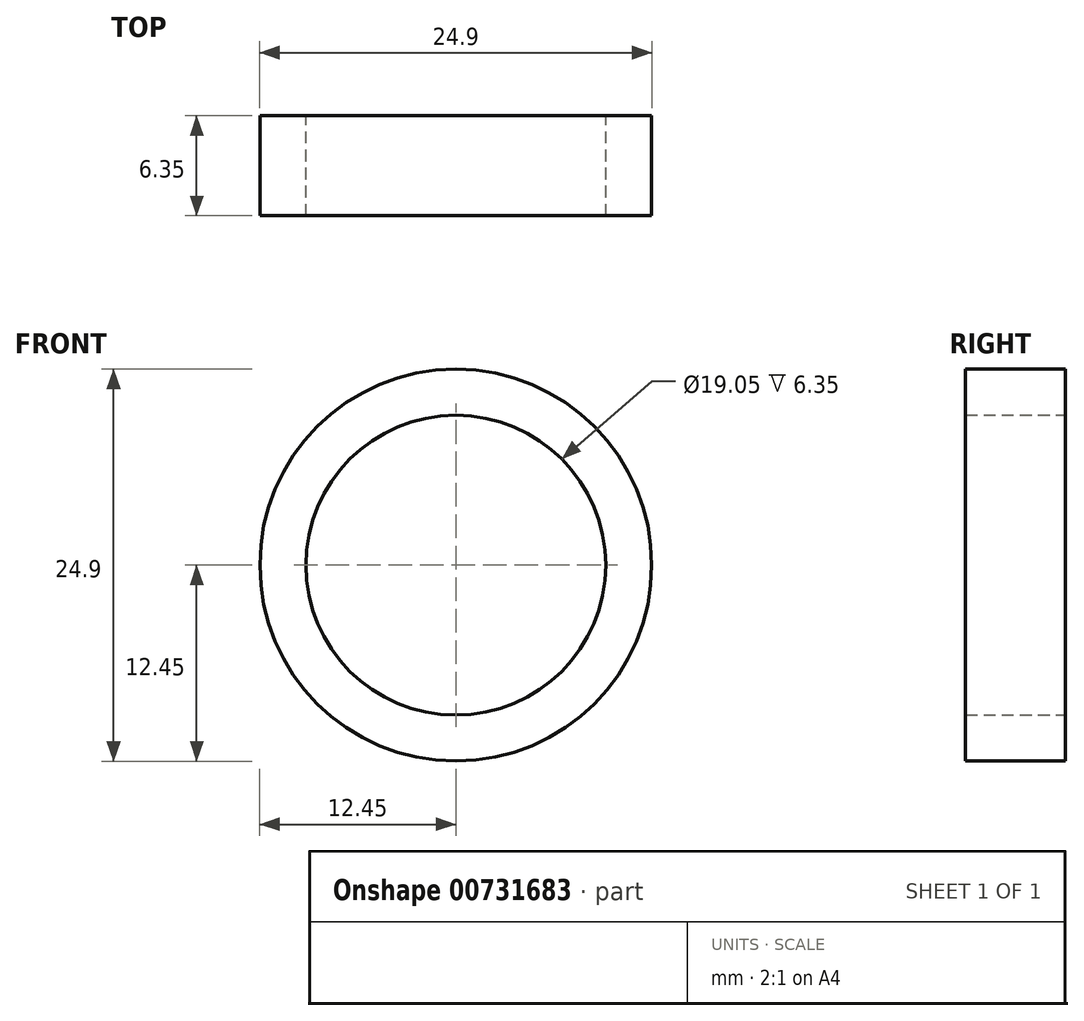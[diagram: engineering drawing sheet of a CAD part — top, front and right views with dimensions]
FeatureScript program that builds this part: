
annotation { "Feature Type Name" : "Feature", "Feature Type Description" : "" }
export const myFeature = defineFeature(function(context is Context, id is Id, definition is map)
    precondition{}
    {
        {
            var Q0;
            Q0=qCreatedBy(makeId("Front.planeOp"),FACE);
            var sketch = newSketch(context, id + "F0", { "sketchPlane" : qUnion([Q0])});
            skCircle(sketch, "E0", {"center": v(0, 0) * mm, "radius": 12.45 * mm});
            skCircle(sketch, "E1", {"center": v(0, 0) * mm, "radius": 9.53 * mm});
            skSolve(sketch);
        }
        {
            var Q0;
            Q0=makeQuery(id+"F0.imprint","IMPRINT",FACE,{"disambiguationData":[TD([[makeQuery(id+"F0.imprint","IMPRINT",EDGE,{"derivedFrom":sQuery(id+"F0.wireOp",EDGE,"E0")}),1.0]])]});
            extrude(context, id + "F1", {"entities" : qUnion([Q0]), "depth" : 6.35 * mm, "offsetDistance" : 25.4 * mm});
        }
    });
